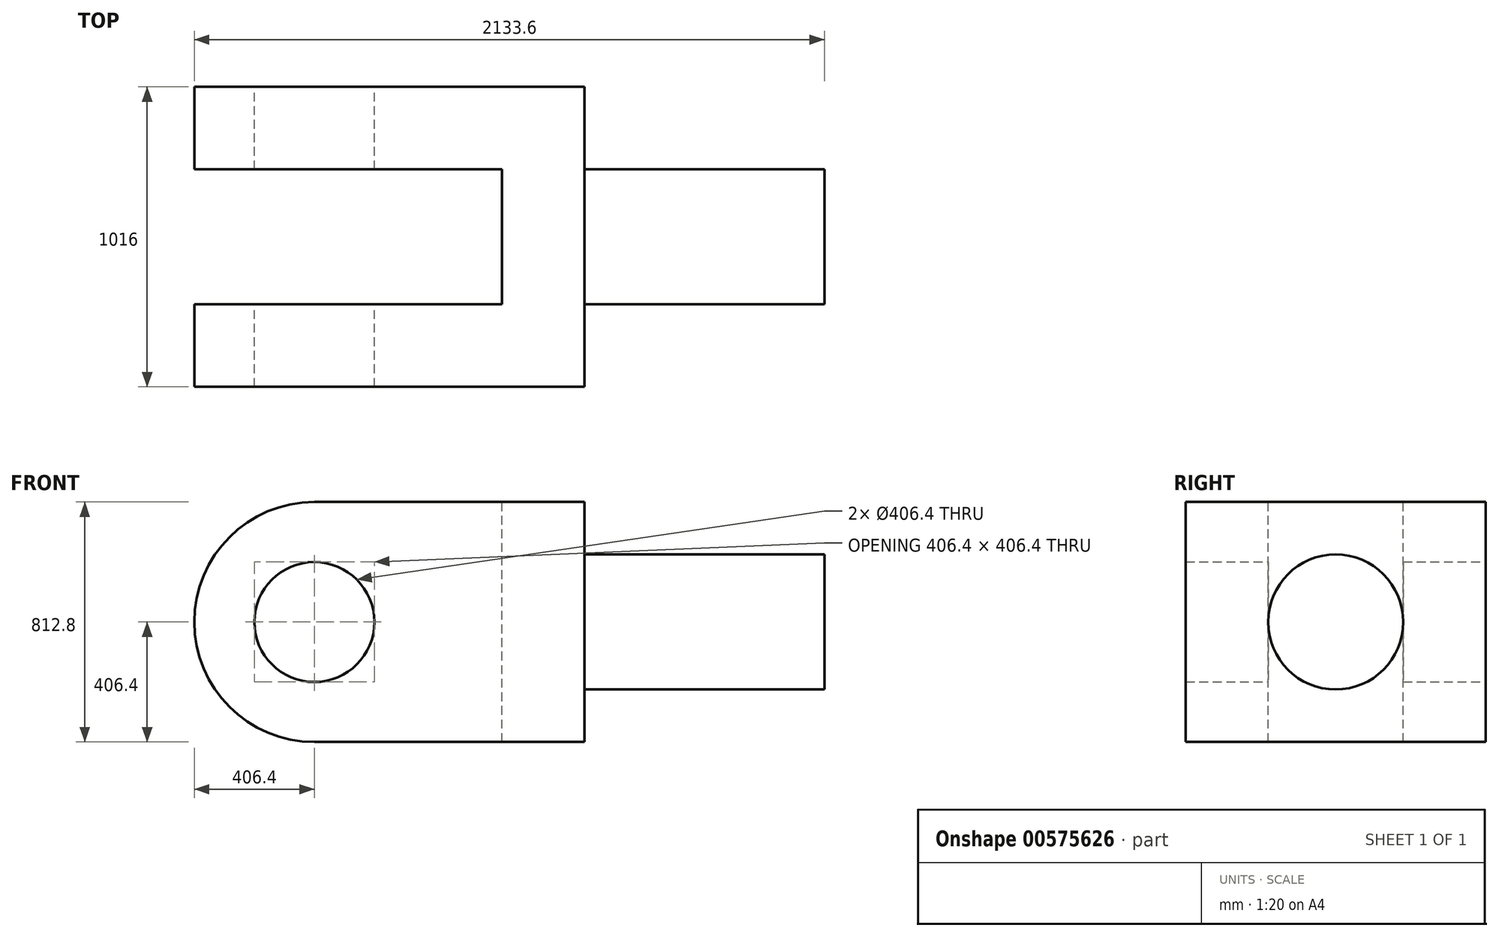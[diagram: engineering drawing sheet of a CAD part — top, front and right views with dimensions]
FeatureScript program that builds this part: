
annotation { "Feature Type Name" : "Feature", "Feature Type Description" : "" }
export const myFeature = defineFeature(function(context is Context, id is Id, definition is map)
    precondition{}
    {
        {
            var Q0;
            Q0=qCreatedBy(makeId("Front.planeOp"),FACE);
            var sketch = newSketch(context, id + "F0", { "sketchPlane" : qUnion([Q0])});
            skCircle(sketch, "E0", {"center": v(0, 0) * mm, "radius": 203.2 * mm});
            skArc(sketch, "E1", {"start": v(0, 406.4) * mm, "mid": v(-406.4, 0) * mm, "end": v(0, -406.4) * mm});
            skLineSegment(sketch, "E2", {"start": v(0, 406.4) * mm, "end": v(914.4, 406.4) * mm});
            skLineSegment(sketch, "E3", {"start": v(914.4, 406.4) * mm, "end": v(914.4, -406.4) * mm});
            skLineSegment(sketch, "E4", {"start": v(914.4, -406.4) * mm, "end": v(0, -406.4) * mm});
            skLineSegment(sketch, "E5.bottom", {"start": v(914.4, 228.6) * mm, "end": v(1727.2, 228.6) * mm});
            skLineSegment(sketch, "E5.top", {"start": v(914.4, -228.6) * mm, "end": v(1727.2, -228.6) * mm});
            skLineSegment(sketch, "E5.left", {"start": v(914.4, 228.6) * mm, "end": v(914.4, -228.6) * mm});
            skLineSegment(sketch, "E5.right", {"start": v(1727.2, 228.6) * mm, "end": v(1727.2, -228.6) * mm});
            skSolve(sketch);
        }
        {
            var Q0;
            Q0=makeQuery(id+"F0.imprint","IMPRINT",FACE,{"disambiguationData":[TD([[makeQuery(id+"F0.imprint","IMPRINT",EDGE,{"derivedFrom":sQuery(id+"F0.wireOp",EDGE,"E0")}),-1.0]])]});
            var Q1;
            Q1=makeQuery(id+"F0.imprint","IMPRINT",FACE,{"disambiguationData":[TD([[makeQuery(id+"F0.imprint","IMPRINT",EDGE,{"derivedFrom":sQuery(id+"F0.wireOp",EDGE,"E5.bottom")}),-1.0]])]});
            extrude(context, id + "F1", {"entities" : qUnion([Q0, Q1]), "depth" : 1016 * mm, "offsetDistance" : 25.4 * mm});
        }
        {
            var Q0;
            Q0=makeQuery(id+"F1.opExtrude","SWEPT_FACE",FACE,{"disambiguationData":[OSD([sQuery(id+"F0.wireOp",EDGE,"E2")])]});
            var sketch = newSketch(context, id + "F2", { "sketchPlane" : qUnion([Q0])});
            skLineSegment(sketch, "E6.bottom", {"start": v(635, -279.4) * mm, "end": v(-406.4, -279.4) * mm});
            skLineSegment(sketch, "E6.top", {"start": v(635, -736.6) * mm, "end": v(-406.4, -736.6) * mm});
            skLineSegment(sketch, "E6.left", {"start": v(635, -279.4) * mm, "end": v(635, -736.6) * mm});
            skLineSegment(sketch, "E6.right", {"start": v(-406.4, -279.4) * mm, "end": v(-406.4, -736.6) * mm});
            skSolve(sketch);
        }
        {
            var Q0;
            {var subQ0=sQuery(id+"F2.wireOp",EDGE,"E6.left");Q0=makeQuery(id+"F2.imprint","IMPRINT",FACE,{"disambiguationData":[TD([[makeQuery(id+"F2.imprint","IMPRINT",EDGE,{"derivedFrom":subQ0}),-1.0]])]});}
            var Q1;
            {var subQ0=sQuery(id+"F2.wireOp",EDGE,"E6.right");Q1=makeQuery(id+"F2.imprint","IMPRINT",FACE,{"disambiguationData":[TD([[makeQuery(id+"F2.imprint","IMPRINT",EDGE,{"derivedFrom":subQ0}),1.0]])]});}
            extrude(context, id + "F3", {"entities" : qUnion([Q0, Q1]), "operationType" : NewBodyOperationType.REMOVE, "endBound" : BoundingType.THROUGH_ALL, "oppositeDirection" : true, "depth" : 25.4 * mm, "offsetDistance" : 25.4 * mm});
        }
        {
            var Q0;
            Q0=makeQuery(id+"F1.opExtrude","SWEPT_FACE",FACE,{"disambiguationData":[OSD([sQuery(id+"F0.wireOp",EDGE,"E5.right")])]});
            var sketch = newSketch(context, id + "F4", { "sketchPlane" : qUnion([Q0])});
            skCircle(sketch, "E7", {"center": v(-508, 0) * mm, "radius": 228.6 * mm});
            skSolve(sketch);
        }
        {
            var Q0;
            {var subQ1=sQuery(id+"F0.wireOp",EDGE,"E5.right");var subQ6=makeQuery(id+"F1.opExtrude","CAP_EDGE",EDGE,{"disambiguationData":[OSD([subQ1])],"isStart":false});Q0=makeQuery(id+"F4.imprint","IMPRINT",FACE,{"disambiguationData":[TD([[makeQuery(id+"F4.imprint","IMPRINT",EDGE,{"derivedFrom":subQ6}),1.0]])]});}
            var Q1;
            {var subQ1=sQuery(id+"F0.wireOp",EDGE,"E5.right");var subQ6=makeQuery(id+"F1.opExtrude","CAP_EDGE",EDGE,{"disambiguationData":[OSD([subQ1])],"isStart":true});Q1=makeQuery(id+"F4.imprint","IMPRINT",FACE,{"disambiguationData":[TD([[makeQuery(id+"F4.imprint","IMPRINT",EDGE,{"derivedFrom":subQ6}),-1.0]])]});}
            extrude(context, id + "F5", {"entities" : qUnion([Q0, Q1]), "operationType" : NewBodyOperationType.REMOVE, "oppositeDirection" : true, "depth" : 812.8 * mm, "offsetDistance" : 25.4 * mm});
        }
    });
